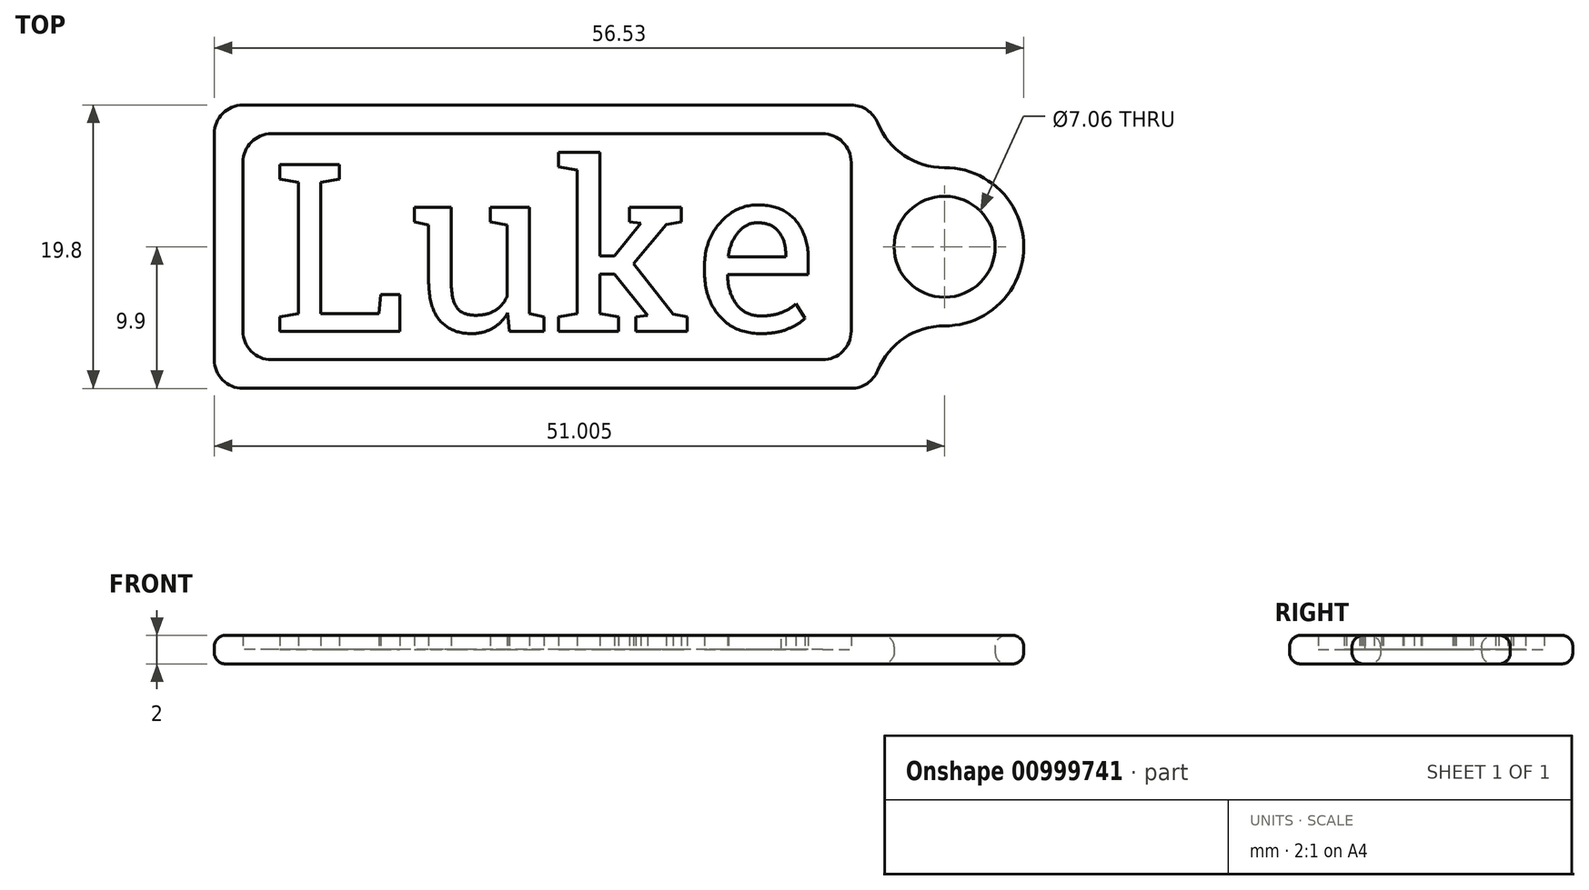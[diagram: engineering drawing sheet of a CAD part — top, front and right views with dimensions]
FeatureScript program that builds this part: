
annotation { "Feature Type Name" : "Feature", "Feature Type Description" : "" }
export const myFeature = defineFeature(function(context is Context, id is Id, definition is map)
    precondition{}
    {
        {
            var Q0;
            Q0=qCreatedBy(makeId("Top.planeOp"),FACE);
            var sketch = newSketch(context, id + "F0", { "sketchPlane" : qUnion([Q0])});
            skText(sketch, "E0", { "text": "Luke", "fontName": "RobotoSlab-Regular.ttf"});
            skLineSegment(sketch, "E1.bottom", {"start": v(-21.18, -7.9) * mm, "end": v(21.3, -7.9) * mm});
            skLineSegment(sketch, "E1.top", {"start": v(-21.18, 7.9) * mm, "end": v(21.3, 7.9) * mm});
            skLineSegment(sketch, "E1.left", {"start": v(-21.18, -7.9) * mm, "end": v(-21.18, 7.9) * mm});
            skLineSegment(sketch, "E1.right", {"start": v(21.3, -7.9) * mm, "end": v(21.3, 7.9) * mm});
            skLineSegment(sketch, "E2.0", {"start": v(-23.18, 9.9) * mm, "end": v(23.3, 9.9) * mm});
            skLineSegment(sketch, "E2.1", {"start": v(-23.18, -9.9) * mm, "end": v(-23.18, 9.9) * mm});
            skLineSegment(sketch, "E2.2", {"start": v(-23.18, -9.9) * mm, "end": v(23.3, -9.9) * mm});
            skLineSegment(sketch, "E2.3", {"start": v(23.3, -9.9) * mm, "end": v(23.3, 9.9) * mm});
            skCircle(sketch, "E3", {"center": v(27.82, 0) * mm, "radius": 3.53 * mm});
            skPoint(sketch, "E3.centerSnap0", {"position": v(23.3, 0) * mm});
            skCircle(sketch, "E4", {"center": v(27.82, 0) * mm, "radius": 5.53 * mm});
            const initialGuessF0  = {"E0": [-0.01918, -0.0059, 1, 0, 0.0118]};
            skSetInitialGuess(sketch, initialGuessF0);
            skSolve(sketch);
        }
        {
            var Q0;
            Q0=makeQuery(id+"F0.imprint","IMPRINT",FACE,{"disambiguationData":[TD([[makeQuery(id+"F0.imprint","IMPRINT",EDGE,{"derivedFrom":sQuery(id+"F0.wireOp",EDGE,"E1.bottom")}),-1.0]])]});
            var Q1;
            Q1=makeQuery(id+"F0.imprint","IMPRINT",FACE,{"disambiguationData":[TD([[makeQuery(id+"F0.imprint","IMPRINT",EDGE,{"derivedFrom":sQuery(id+"F0.wireOp",EDGE,"E0.sketch_text.stroke-0")}),1.0]])]});
            var Q2;
            Q2=makeQuery(id+"F0.imprint","IMPRINT",FACE,{"disambiguationData":[TD([[makeQuery(id+"F0.imprint","IMPRINT",EDGE,{"derivedFrom":sQuery(id+"F0.wireOp",EDGE,"E0.sketch_text.stroke-84")}),1.0]])]});
            extrude(context, id + "F1", {"entities" : qUnion([Q0, Q1, Q2]), "depth" : 1 * mm, "offsetDistance" : 25 * mm});
        }
        {
            var Q0;
            Q0=makeQuery(id+"F0.imprint","IMPRINT",FACE,{"disambiguationData":[TD([[makeQuery(id+"F0.imprint","IMPRINT",EDGE,{"derivedFrom":sQuery(id+"F0.wireOp",EDGE,"E1.bottom")}),-1.0]])]});
            var Q1;
            Q1=makeQuery(id+"F0.imprint","IMPRINT",FACE,{"disambiguationData":[TD([[makeQuery(id+"F0.imprint","IMPRINT",EDGE,{"derivedFrom":sQuery(id+"F0.wireOp",EDGE,"E0.sketch_text.stroke-0")}),-1.0]])]});
            var Q2;
            Q2=makeQuery(id+"F0.imprint","IMPRINT",FACE,{"disambiguationData":[TD([[makeQuery(id+"F0.imprint","IMPRINT",EDGE,{"derivedFrom":sQuery(id+"F0.wireOp",EDGE,"E0.sketch_text.stroke-16")}),-1.0]])]});
            var Q3;
            Q3=makeQuery(id+"F0.imprint","IMPRINT",FACE,{"disambiguationData":[TD([[makeQuery(id+"F0.imprint","IMPRINT",EDGE,{"derivedFrom":sQuery(id+"F0.wireOp",EDGE,"E0.sketch_text.stroke-40")}),-1.0]])]});
            var Q4;
            Q4=makeQuery(id+"F0.imprint","IMPRINT",FACE,{"disambiguationData":[TD([[makeQuery(id+"F0.imprint","IMPRINT",EDGE,{"derivedFrom":sQuery(id+"F0.wireOp",EDGE,"E0.sketch_text.stroke-67")}),-1.0]])]});
            var Q5;
            Q5=makeQuery(id+"F0.imprint","IMPRINT",FACE,{"disambiguationData":[TD([[makeQuery(id+"F0.imprint","IMPRINT",EDGE,{"derivedFrom":sQuery(id+"F0.wireOp",EDGE,"E3")}),-1.0]])]});
            var Q6;
            {var subQ0=sQuery(id+"F0.wireOp",EDGE,"E4");var subQ1=sQuery(id+"F0.wireOp",EDGE,"E2.3");var subQ2=makeQuery(id+"F0.imprint","INTERSECT",VERTEX,{"disambiguationData":[OD(0.0)],"derivedFrom":[subQ1,subQ0]});Q6=makeQuery(id+"F0.imprint","IMPRINT",FACE,{"disambiguationData":[TD([[makeQuery(id+"F0.imprint","IMPRINT",EDGE,{"disambiguationData":[TD([[subQ2,-1.0]])],"derivedFrom":subQ1}),1.0]])]});}
            extrude(context, id + "F2", {"entities" : qUnion([Q0, Q1, Q2, Q3, Q4, Q5, Q6]), "operationType" : NewBodyOperationType.ADD, "depth" : 2 * mm, "offsetDistance" : 25 * mm});
        }
        {
            var Q0;
            {var subQ0=sQuery(id+"F0.wireOp",EDGE,"E2.1");var subQ1=sQuery(id+"F0.wireOp",EDGE,"E2.0");Q0=makeQuery(id+"F2.boolean.opBoolean","MERGE",EDGE,{"derivedFrom":[makeQuery(id+"F1.opExtrude","SWEPT_EDGE",EDGE,{"disambiguationData":[OSD([subQ1,subQ0])]}),makeQuery(id+"F2.opExtrude","SWEPT_EDGE",EDGE,{"disambiguationData":[OSD([subQ1,subQ0])]})]});}
            var Q1;
            {var subQ0=sQuery(id+"F0.wireOp",EDGE,"E2.2");var subQ1=sQuery(id+"F0.wireOp",EDGE,"E2.1");Q1=makeQuery(id+"F2.boolean.opBoolean","MERGE",EDGE,{"derivedFrom":[makeQuery(id+"F1.opExtrude","SWEPT_EDGE",EDGE,{"disambiguationData":[OSD([subQ1,subQ0])]}),makeQuery(id+"F2.opExtrude","SWEPT_EDGE",EDGE,{"disambiguationData":[OSD([subQ1,subQ0])]})]});}
            var Q2;
            {var subQ0=sQuery(id+"F0.wireOp",EDGE,"E2.3");var subQ1=sQuery(id+"F0.wireOp",EDGE,"E2.2");Q2=makeQuery(id+"F2.boolean.opBoolean","MERGE",EDGE,{"derivedFrom":[makeQuery(id+"F1.opExtrude","SWEPT_EDGE",EDGE,{"disambiguationData":[OSD([subQ1,subQ0])]}),makeQuery(id+"F2.opExtrude","SWEPT_EDGE",EDGE,{"disambiguationData":[OSD([subQ1,subQ0])]})]});}
            var Q3;
            {var subQ0=sQuery(id+"F0.wireOp",EDGE,"E2.3");var subQ1=sQuery(id+"F0.wireOp",EDGE,"E2.0");Q3=makeQuery(id+"F2.boolean.opBoolean","MERGE",EDGE,{"derivedFrom":[makeQuery(id+"F1.opExtrude","SWEPT_EDGE",EDGE,{"disambiguationData":[OSD([subQ1,subQ0])]}),makeQuery(id+"F2.opExtrude","SWEPT_EDGE",EDGE,{"disambiguationData":[OSD([subQ1,subQ0])]})]});}
            var Q4;
            Q4=makeQuery(id+"F2.opExtrude","SWEPT_EDGE",EDGE,{"disambiguationData":[OSD([sQuery(id+"F0.wireOp",EDGE,"E1.top"),sQuery(id+"F0.wireOp",EDGE,"E1.left")])]});
            var Q5;
            Q5=makeQuery(id+"F2.opExtrude","SWEPT_EDGE",EDGE,{"disambiguationData":[OSD([sQuery(id+"F0.wireOp",EDGE,"E1.top"),sQuery(id+"F0.wireOp",EDGE,"E1.right")])]});
            var Q6;
            Q6=makeQuery(id+"F2.opExtrude","SWEPT_EDGE",EDGE,{"disambiguationData":[OSD([sQuery(id+"F0.wireOp",EDGE,"E1.bottom"),sQuery(id+"F0.wireOp",EDGE,"E1.left")])]});
            var Q7;
            Q7=makeQuery(id+"F2.opExtrude","SWEPT_EDGE",EDGE,{"disambiguationData":[OSD([sQuery(id+"F0.wireOp",EDGE,"E1.bottom"),sQuery(id+"F0.wireOp",EDGE,"E1.right")])]});
            fillet(context, id + "F3", {"entities" : qUnion([Q0, Q1, Q2, Q3, Q4, Q5, Q6, Q7]), "radius" : 2 * mm, "tangentPropagation" : true, "allowEdgeOverflow" : false});
        }
        {
            var Q0;
            {var subQ0=sQuery(id+"F0.wireOp",EDGE,"E4");var subQ1=sQuery(id+"F0.wireOp",EDGE,"E2.3");var subQ2=makeQuery(id+"F0.imprint","INTERSECT",VERTEX,{"disambiguationData":[OD(1.0)],"derivedFrom":[subQ1,subQ0]});Q0=makeQuery(id+"F2.boolean.opBoolean","MERGE",EDGE,{"derivedFrom":[makeQuery(id+"F1.opExtrude","SWEPT_EDGE",EDGE,{"disambiguationData":[OSD([subQ1,subQ0]),TDD([subQ2])]}),makeQuery(id+"F2.opExtrude","SWEPT_EDGE",EDGE,{"disambiguationData":[OSD([subQ1,subQ0]),TDD([subQ2])]})]});}
            var Q1;
            {var subQ0=sQuery(id+"F0.wireOp",EDGE,"E4");var subQ1=sQuery(id+"F0.wireOp",EDGE,"E2.3");var subQ2=makeQuery(id+"F0.imprint","INTERSECT",VERTEX,{"disambiguationData":[OD(0.0)],"derivedFrom":[subQ1,subQ0]});Q1=makeQuery(id+"F2.boolean.opBoolean","MERGE",EDGE,{"derivedFrom":[makeQuery(id+"F1.opExtrude","SWEPT_EDGE",EDGE,{"disambiguationData":[OSD([subQ1,subQ0]),TDD([subQ2])]}),makeQuery(id+"F2.opExtrude","SWEPT_EDGE",EDGE,{"disambiguationData":[OSD([subQ1,subQ0]),TDD([subQ2])]})]});}
            fillet(context, id + "F4", {"entities" : qUnion([Q0, Q1]), "radius" : 5 * mm, "tangentPropagation" : true, "allowEdgeOverflow" : false});
        }
        {
            var Q0;
            Q0=makeQuery(id+"F2.opExtrude","CAP_EDGE",EDGE,{"disambiguationData":[OSD([sQuery(id+"F0.wireOp",EDGE,"E2.0")])],"isStart":false});
            var Q1;
            Q1=makeQuery(id+"F1.opExtrude","CAP_EDGE",EDGE,{"disambiguationData":[OSD([sQuery(id+"F0.wireOp",EDGE,"E2.2")])],"isStart":true});
            var Q2;
            Q2=makeQuery(id+"F2.opExtrude","CAP_EDGE",EDGE,{"disambiguationData":[OSD([sQuery(id+"F0.wireOp",EDGE,"E3")])],"isStart":false});
            var Q3;
            Q3=makeQuery(id+"F2.opExtrude","CAP_EDGE",EDGE,{"disambiguationData":[OSD([sQuery(id+"F0.wireOp",EDGE,"E3")])],"isStart":true});
            fillet(context, id + "F5", {"entities" : qUnion([Q0, Q1, Q2, Q3]), "radius" : .8 * mm, "tangentPropagation" : true, "allowEdgeOverflow" : false});
        }
    });
